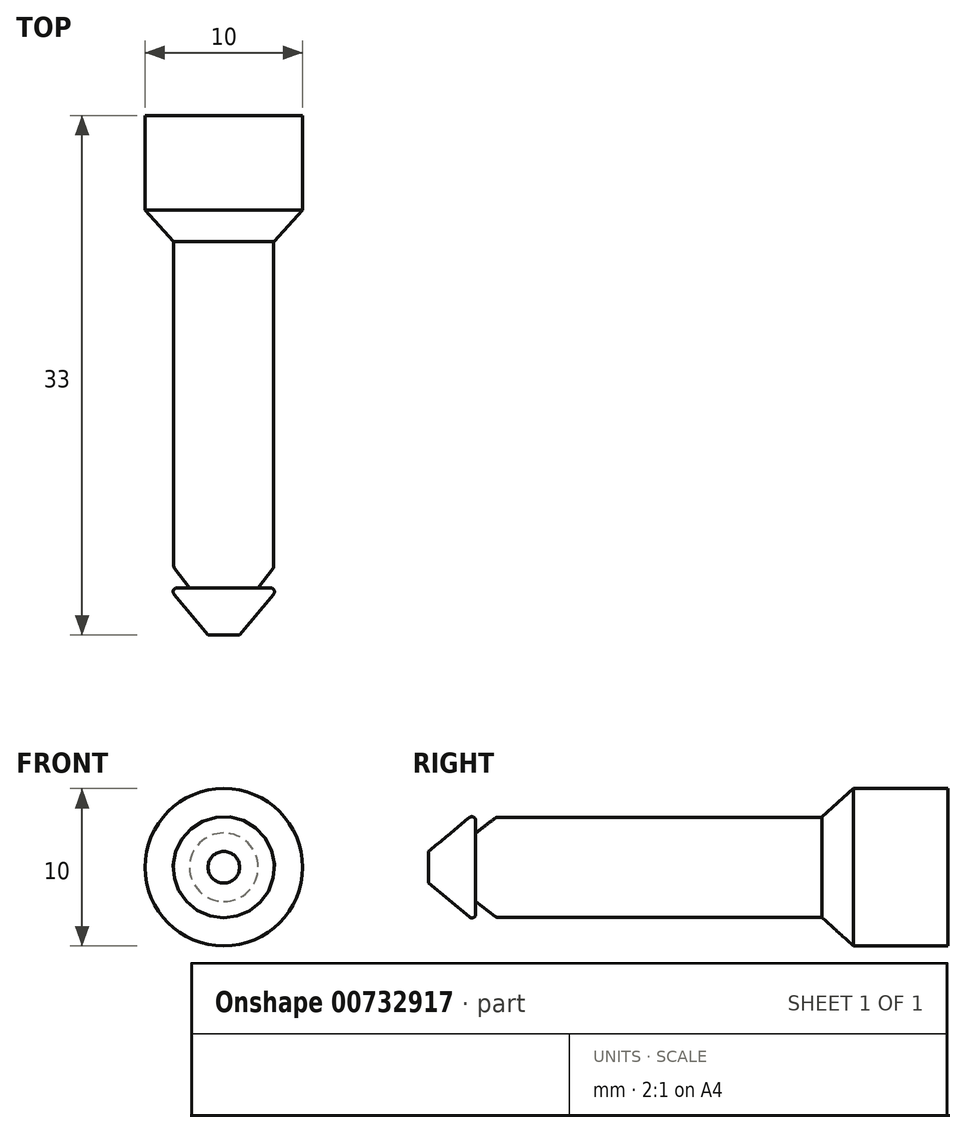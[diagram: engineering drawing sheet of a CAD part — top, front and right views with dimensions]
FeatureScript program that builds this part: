
annotation { "Feature Type Name" : "Feature", "Feature Type Description" : "" }
export const myFeature = defineFeature(function(context is Context, id is Id, definition is map)
    precondition{}
    {
        {
            var Q0;
            Q0=qCreatedBy(makeId("Front.planeOp"),FACE);
            var sketch = newSketch(context, id + "F0", { "sketchPlane" : qUnion([Q0])});
            skCircle(sketch, "E0", {"center": v(0, 0) * mm, "radius": 5 * mm});
            skSolve(sketch);
        }
        {
            var Q0;
            Q0 = qSketchRegion(id + "F0", true);
            extrude(context, id + "F1", {"entities" : qUnion([Q0]), "depth" : 3 * mm, "offsetDistance" : 25 * mm});
        }
        {
            var Q0;
            Q0=makeQuery(id+"F1.opExtrude","CAP_FACE",FACE,{"disambiguationData":[OSD([sQuery(id+"F0.wireOp",EDGE,"E0")])],"isStart":false});
            var sketch = newSketch(context, id + "F2", { "sketchPlane" : qUnion([Q0])});
            skCircle(sketch, "E1", {"center": v(0, 0) * mm, "radius": 3.17 * mm});
            skSolve(sketch);
        }
        {
            var Q0;
            Q0 = qSketchRegion(id + "F2", true);
            extrude(context, id + "F3", {"entities" : qUnion([Q0]), "operationType" : NewBodyOperationType.ADD, "depth" : 22 * mm, "offsetDistance" : 25 * mm});
        }
        {
            var Q0;
            Q0=makeQuery(id+"F3.opExtrude","CAP_EDGE",EDGE,{"disambiguationData":[OSD([sQuery(id+"F2.wireOp",EDGE,"E1")])],"isStart":false});
            chamfer(context, id + "F4", {"entities" : qUnion([Q0]), "chamferType" : ChamferType.TWO_OFFSETS, "width1" : 1 * mm, "oppositeDirection" : false, "width2" : 1.3 * mm, "tangentPropagation" : true});
        }
        {
            var Q0;
            Q0=makeQuery(id+"F3.opExtrude","CAP_FACE",FACE,{"disambiguationData":[OSD([sQuery(id+"F2.wireOp",EDGE,"E1")])],"isStart":false});
            var sketch = newSketch(context, id + "F5", { "sketchPlane" : qUnion([Q0])});
            skCircle(sketch, "E2", {"center": v(0, 0) * mm, "radius": 3.5 * mm});
            skSolve(sketch);
        }
        {
            var Q0;
            Q0 = qSketchRegion(id + "F5", true);
            extrude(context, id + "F6", {"entities" : qUnion([Q0]), "operationType" : NewBodyOperationType.ADD, "depth" : 3 * mm, "offsetDistance" : 25 * mm});
        }
        {
            var Q0;
            Q0=makeQuery(id+"F6.opExtrude","CAP_EDGE",EDGE,{"disambiguationData":[OSD([sQuery(id+"F5.wireOp",EDGE,"E2")])],"isStart":false});
            chamfer(context, id + "F7", {"entities" : qUnion([Q0]), "chamferType" : ChamferType.TWO_OFFSETS, "width1" : 2.5 * mm, "oppositeDirection" : false, "width2" : 3 * mm, "tangentPropagation" : true});
        }
        {
            var Q0;
            {var subQ0=sQuery(id+"F5.wireOp",EDGE,"E2");Q0=makeQuery(id+"F7.opChamfer","BLEND_EDGE",EDGE,{"blendedFrom":[makeQuery(id+"F6.opExtrude","CAP_EDGE",EDGE,{"disambiguationData":[OSD([subQ0])],"isStart":false}),makeQuery(id+"F6.opExtrude","CAP_FACE",FACE,{"disambiguationData":[OSD([subQ0])],"isStart":true})],"blendedInto":[makeQuery(id+"F6.opExtrude","CAP_FACE",FACE,{"disambiguationData":[OSD([subQ0])],"isStart":true})]});}
            var Q1;
            {var subQ0=sQuery(id+"F2.wireOp",EDGE,"E1");Q1=makeQuery(id+"F4.opChamfer","BLEND_EDGE",EDGE,{"blendedFrom":[makeQuery(id+"F3.opExtrude","CAP_EDGE",EDGE,{"disambiguationData":[OSD([subQ0])],"isStart":false}),makeQuery(id+"F3.opExtrude","SWEPT_FACE",FACE,{"disambiguationData":[OSD([subQ0])]})],"blendedInto":[makeQuery(id+"F3.opExtrude","SWEPT_FACE",FACE,{"disambiguationData":[OSD([subQ0])]})]});}
            fillet(context, id + "F8", {"entities" : qUnion([Q0, Q1]), "radius" : 0.25 * mm, "tangentPropagation" : true, "allowEdgeOverflow" : false});
        }
        {
            var Q0;
            Q0=makeQuery(id+"F1.opExtrude","CAP_EDGE",EDGE,{"disambiguationData":[OSD([sQuery(id+"F0.wireOp",EDGE,"E0")])],"isStart":false});
            chamfer(context, id + "F9", {"entities" : qUnion([Q0]), "chamferType" : ChamferType.TWO_OFFSETS, "width1" : 1.8 * mm, "oppositeDirection" : false, "width2" : 2 * mm, "tangentPropagation" : true});
        }
        {
            var Q0;
            Q0=makeQuery(id+"F1.opExtrude","CAP_FACE",FACE,{"disambiguationData":[OSD([sQuery(id+"F0.wireOp",EDGE,"E0")])],"isStart":true});
            extrude(context, id + "F10", {"entities" : qUnion([Q0]), "operationType" : NewBodyOperationType.ADD, "depth" : 5 * mm, "offsetDistance" : 25 * mm});
        }
    });
